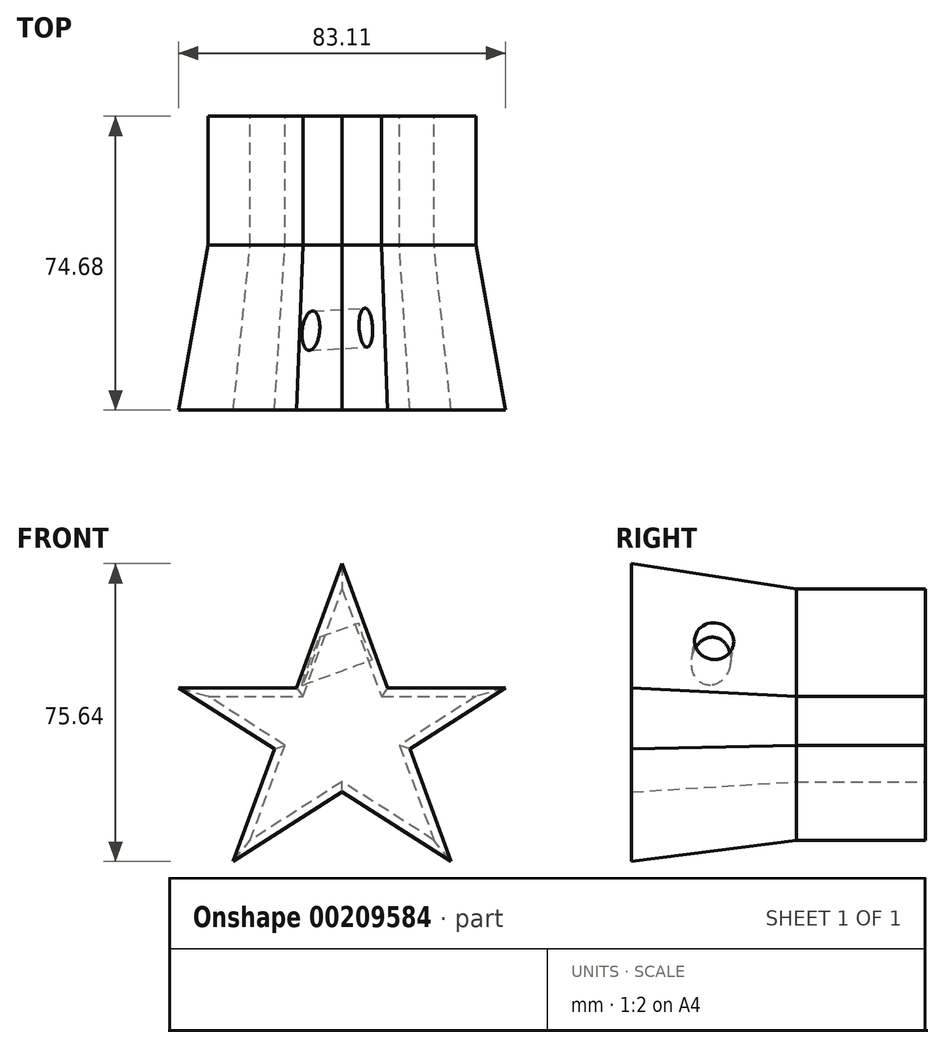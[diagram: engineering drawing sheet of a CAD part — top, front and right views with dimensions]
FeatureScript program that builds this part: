
annotation { "Feature Type Name" : "Feature", "Feature Type Description" : "" }
export const myFeature = defineFeature(function(context is Context, id is Id, definition is map)
    precondition{}
    {
        {
            var Q0;
            Q0=qCreatedBy(makeId("Front.planeOp"),FACE);
            var sketch = newSketch(context, id + "F0", { "sketchPlane" : qUnion([Q0])});
            skLineSegment(sketch, "E0", {"start": v(0, 0) * mm, "end": v(23.36, 63.9) * mm});
            skLineSegment(sketch, "E1", {"start": v(23.36, 63.9) * mm, "end": v(46.73, 0) * mm});
            skLineSegment(sketch, "E2", {"start": v(46.73, 0) * mm, "end": v(-10.66, 36.56) * mm});
            skLineSegment(sketch, "E3", {"start": v(-10.66, 36.56) * mm, "end": v(57.38, 36.56) * mm});
            skLineSegment(sketch, "E4", {"start": v(57.38, 36.56) * mm, "end": v(0, 0) * mm});
            skPoint(sketch, "E5", {"position": v(23.36, 14.88) * mm});
            skSolve(sketch);
        }
        {
            var Q0;
            Q0 = qSketchRegion(id + "F0", true);
            extrude(context, id + "F1", {"entities" : qUnion([Q0]), "depth" : 41.9 * mm, "hasDraft" : true, "draftAngle" : 3 * degree, "hasSecondDirection" : true, "secondDirectionOppositeDirection" : true, "secondDirectionDepth" : 32.77 * mm});
        }
        {
            var Q0;
            {var subQ0=sQuery(id+"F0.wireOp",EDGE,"E1");Q0=makeQuery(id+"F1.*.split.splitOp","SPLIT",FACE,{"derivedFrom":makeQuery(id+"F1.opExtrude","SWEPT_FACE",FACE,{"disambiguationData":[OSD([subQ0]),TDD([makeQuery(id+"F0.imprint","IMPRINT",EDGE,{"disambiguationData":[TD([[makeQuery(id+"F0.imprint","INTERSECT",VERTEX,{"derivedFrom":[sQuery(id+"F0.wireOp",EDGE,"E0"),subQ0]}),-1.0]])],"derivedFrom":subQ0})])]})});}
            var sketch = newSketch(context, id + "F2", { "sketchPlane" : qUnion([Q0])});
            skCircle(sketch, "E6", {"center": v(-23.28, 37.44) * mm, "radius": 4.98 * mm});
            skPoint(sketch, "E6.centerSnap0", {"position": v(-44.26, 37.44) * mm});
            skPoint(sketch, "E7", {"position": v(-2.3, 37.44) * mm});
            skPoint(sketch, "E8", {"position": v(-23.28, 55) * mm});
            skSolve(sketch);
        }
        {
            var Q0;
            Q0=makeQuery(id+"F2.imprint","IMPRINT",FACE,{"disambiguationData":[TD([[makeQuery(id+"F2.imprint","IMPRINT",EDGE,{"derivedFrom":sQuery(id+"F2.wireOp",EDGE,"E6")}),1.0]])]});
            var Q1;
            Q1=sQuery(id+"F2.wireOp",EDGE,"E6");
            var Q2;
            {var subQ0=sQuery(id+"F0.wireOp",EDGE,"E0");Q2=makeQuery(id+"F1.*.split.splitOp","SPLIT",FACE,{"derivedFrom":makeQuery(id+"F1.opExtrude","SWEPT_FACE",FACE,{"disambiguationData":[OSD([subQ0]),TDD([makeQuery(id+"F0.imprint","IMPRINT",EDGE,{"disambiguationData":[TD([[makeQuery(id+"F0.imprint","INTERSECT",VERTEX,{"derivedFrom":[subQ0,sQuery(id+"F0.wireOp",EDGE,"E1")]}),1.0]])],"derivedFrom":subQ0})])]})});}
            extrude(context, id + "F3", {"entities" : qUnion([Q0]), "operationType" : NewBodyOperationType.REMOVE, "surfaceEntities" : qUnion([Q1]), "endBound" : BoundingType.UP_TO_SURFACE, "oppositeDirection" : true, "endBoundEntityFace" : qUnion([Q2]), "depth" : 18.29 * mm});
        }
    });
